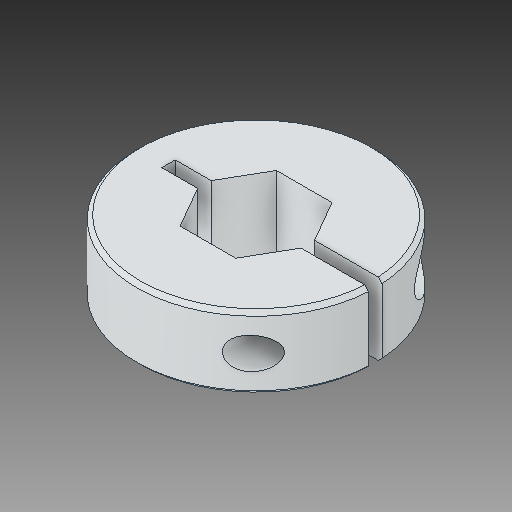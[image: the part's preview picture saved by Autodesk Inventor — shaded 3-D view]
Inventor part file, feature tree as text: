
AUTODESK INVENTOR PART (.ipt)
format: ipt  version: 2017 (Build 210142000, 142)  size: 136,192 bytes
history: native  units: in
note: dims shown in document units (in); Inventor stores cm internally (conversion verified against a paired STEP export)
features: chamfer x1
ambient origin geometry x8: Origin, YZ Plane, XZ Plane, XY Plane, X Axis, Y Axis, Z Axis, Center Point
bodies: Solid1 (feature_tree)
feature tree (1):
  chamfer  "Chamfer1"  [1 undecoded]
note: 1 required parameter value undecoded (feature->parameter linkage not recoverable at this tier; creation-order binding heuristic only, values carry confidence <= 0.55)
